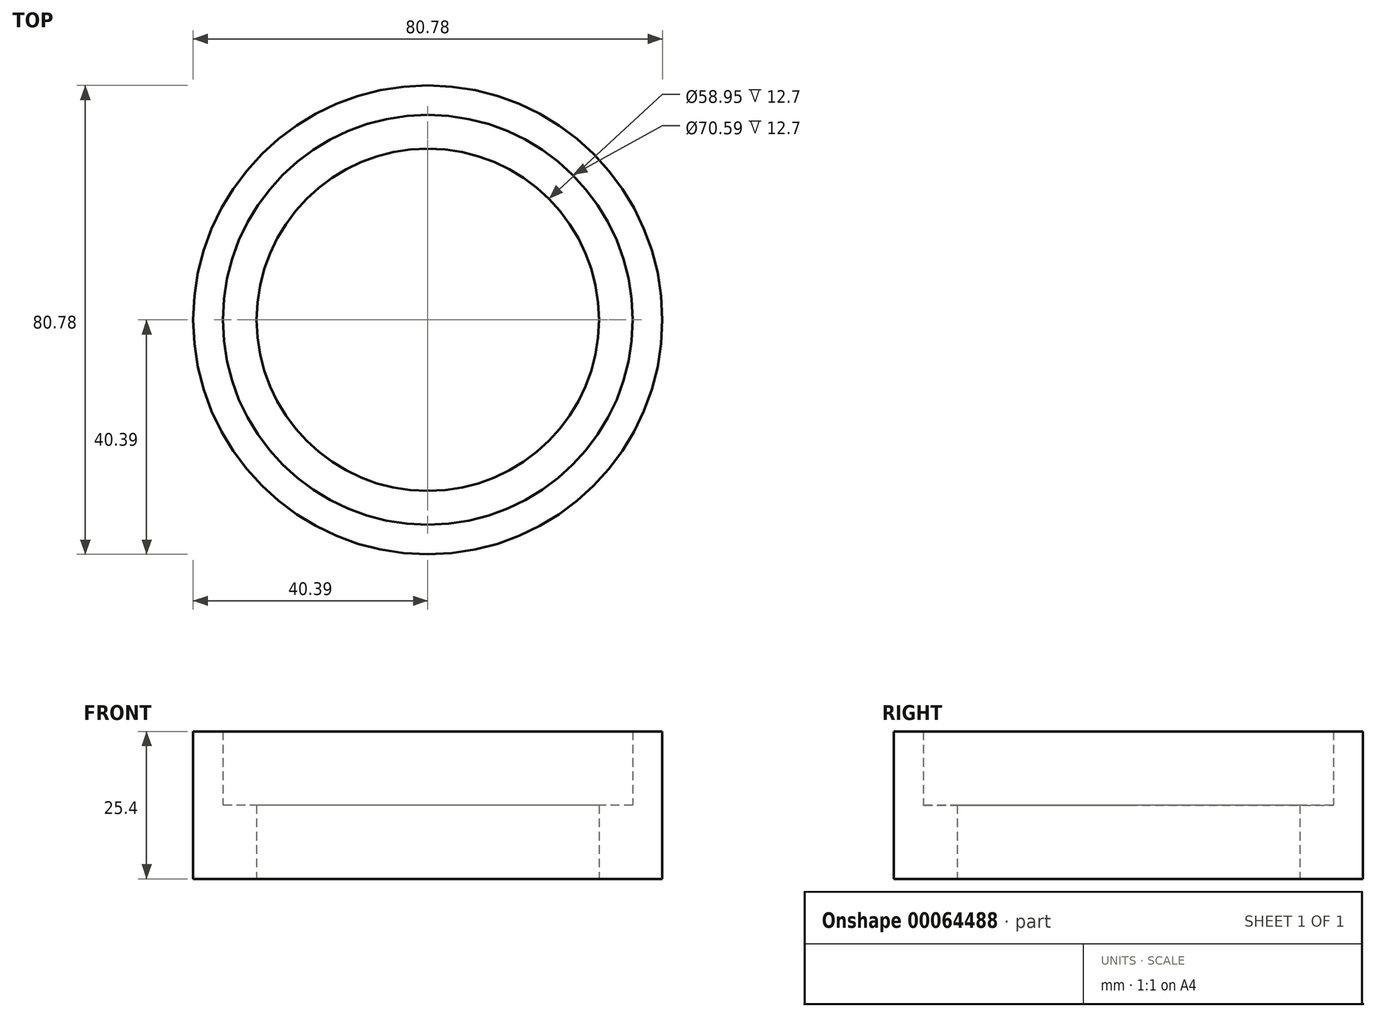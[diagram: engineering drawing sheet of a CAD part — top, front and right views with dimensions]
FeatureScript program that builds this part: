
annotation { "Feature Type Name" : "Feature", "Feature Type Description" : "" }
export const myFeature = defineFeature(function(context is Context, id is Id, definition is map)
    precondition{}
    {
        {
            var Q0;
            Q0=qCreatedBy(makeId("Top.planeOp"),FACE);
            var sketch = newSketch(context, id + "F0", { "sketchPlane" : qUnion([Q0])});
            skCircle(sketch, "E0", {"center": v(0, 0) * mm, "radius": 40.39 * mm});
            skCircle(sketch, "E1", {"center": v(0, 0) * mm, "radius": 35.3 * mm});
            skCircle(sketch, "E2", {"center": v(0, 0) * mm, "radius": 29.48 * mm});
            skSolve(sketch);
        }
        {
            var Q0;
            Q0 = qSketchRegion(id + "F0", true);
            var Q1;
            Q1=makeQuery(id+"F0.imprint","IMPRINT",FACE,{"disambiguationData":[TD([[makeQuery(id+"F0.imprint","IMPRINT",EDGE,{"derivedFrom":sQuery(id+"F0.wireOp",EDGE,"E1")}),1.0]])]});
            extrude(context, id + "F1", {"entities" : qUnion([Q0, Q1]), "depth" : 12.7 * mm});
        }
        {
            var Q0;
            Q0 = qSketchRegion(id + "F0", true);
            extrude(context, id + "F2", {"entities" : qUnion([Q0]), "operationType" : NewBodyOperationType.ADD, "depth" : 25.4 * mm});
        }
    });
